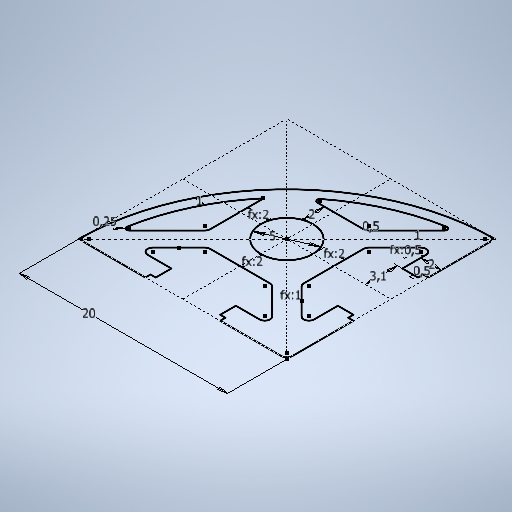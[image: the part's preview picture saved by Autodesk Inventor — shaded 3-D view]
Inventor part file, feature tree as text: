
AUTODESK INVENTOR PART (.ipt)
format: ipt  version: 2025.2 (Build 292293000, 293)  size: 302,592 bytes
history: native  units: mm
features: sketch x1
ambient origin geometry x8: Origin, YZ Plane, XZ Plane, XY Plane, X Axis, Y Axis, Z Axis, Center Point
feature tree (1):
  sketch  "Esboço1"  dims[d5=20.0mm d6=5.0mm d8=2.0mm d9=0.5mm d10=2.0mm d11=1.0mm d12=0.5mm d13=0.5mm d14=3.1mm d15=2.0mm d17=1.0mm d18=2.0mm d20=2.0mm d21=1.0mm d22=0.25mm]
